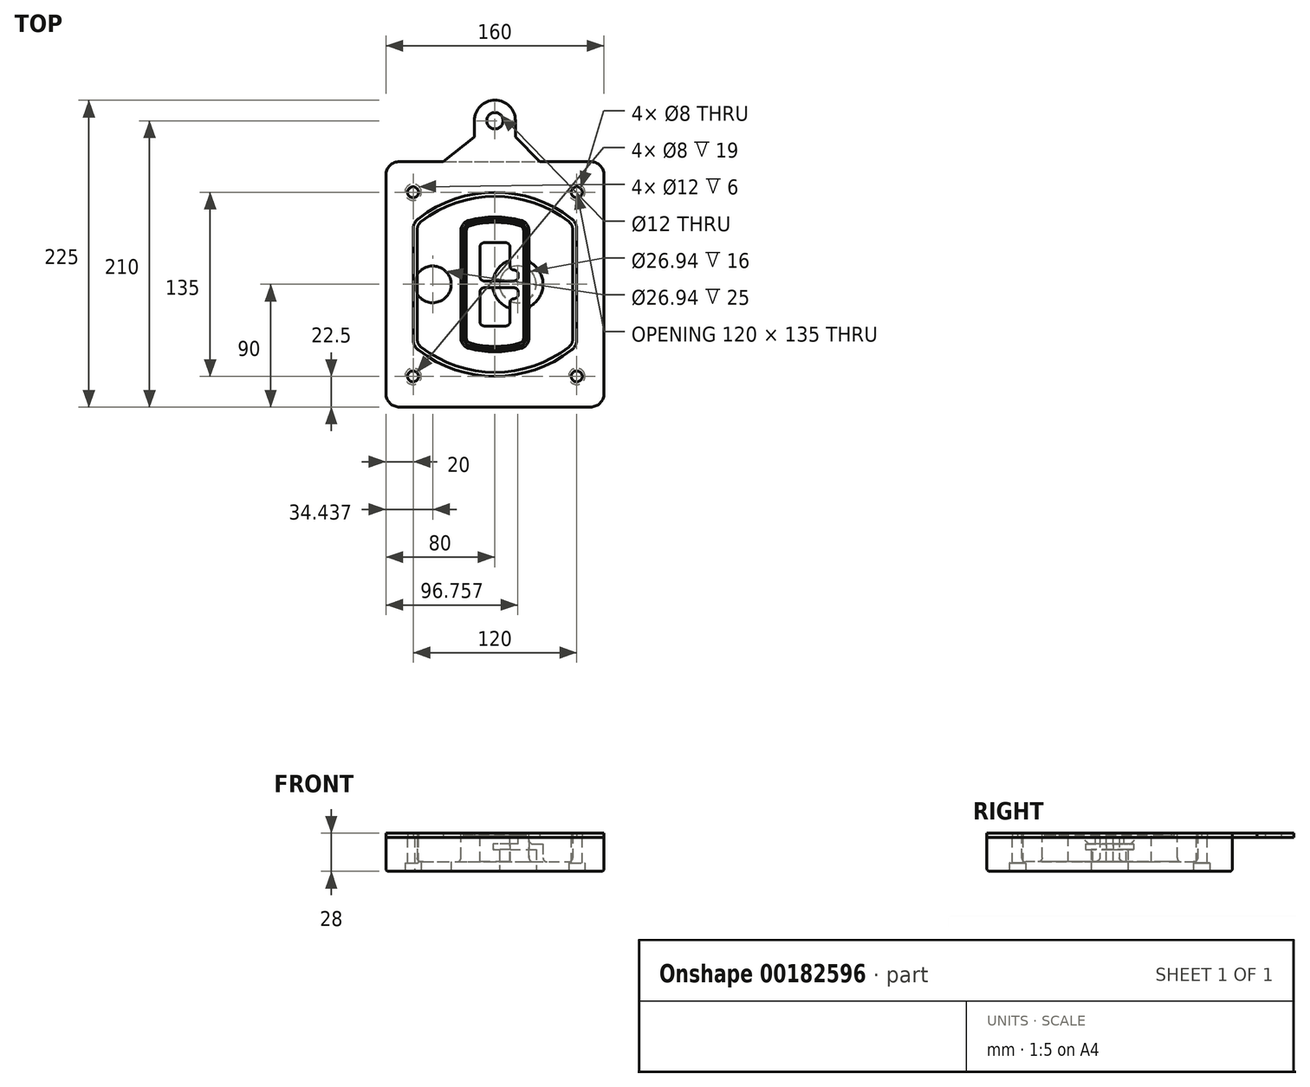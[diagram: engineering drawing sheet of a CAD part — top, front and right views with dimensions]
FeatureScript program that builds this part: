
annotation { "Feature Type Name" : "Feature", "Feature Type Description" : "" }
export const myFeature = defineFeature(function(context is Context, id is Id, definition is map)
    precondition{}
    {
        {
            var Q0;
            Q0=qCreatedBy(makeId("Top.planeOp"),FACE);
            var sketch = newSketch(context, id + "F0", { "sketchPlane" : qUnion([Q0])});
            skPoint(sketch, "E0.rect.middle", {"position": v(0, 0) * mm});
            skLineSegment(sketch, "E1.bottom", {"start": v(-70, -90) * mm, "end": v(70, -90) * mm});
            skLineSegment(sketch, "E1.top", {"start": v(-70, 90) * mm, "end": v(70, 90) * mm});
            skLineSegment(sketch, "E1.left", {"start": v(-80, -80) * mm, "end": v(-80, 80) * mm});
            skLineSegment(sketch, "E1.right", {"start": v(80, -80) * mm, "end": v(80, 80) * mm});
            skLineSegment(sketch, "E2", {"start": v(-80, 90) * mm, "end": v(80, -90) * mm, "construction": true});
            skLineSegment(sketch, "E3", {"start": v(80, 90) * mm, "end": v(-80, -90) * mm, "construction": true});
            skCircle(sketch, "E4", {"center": v(-60, 67.5) * mm, "radius": 4 * mm});
            skCircle(sketch, "E5", {"center": v(60, 67.5) * mm, "radius": 4 * mm});
            skCircle(sketch, "E6", {"center": v(60, -67.5) * mm, "radius": 4 * mm});
            skCircle(sketch, "E7", {"center": v(-60, -67.5) * mm, "radius": 4 * mm});
            skLineSegment(sketch, "E8", {"start": v(-60, 67.5) * mm, "end": v(60, 67.5) * mm, "construction": true});
            skLineSegment(sketch, "E9", {"start": v(60, 67.5) * mm, "end": v(60, -67.5) * mm, "construction": true});
            skLineSegment(sketch, "E10", {"start": v(60, -67.5) * mm, "end": v(-60, -67.5) * mm, "construction": true});
            skLineSegment(sketch, "E11", {"start": v(-60, -67.5) * mm, "end": v(-60, 67.5) * mm, "construction": true});
            skLineSegment(sketch, "E12", {"start": v(-60, 40.3) * mm, "end": v(-60, -40.3) * mm});
            skLineSegment(sketch, "E13", {"start": v(60, 40.3) * mm, "end": v(60, -40.3) * mm});
            skArc(sketch, "E14", {"start": v(56.15, 48.18) * mm, "mid": v(0, 67.5) * mm, "end": v(-56.15, 48.18) * mm});
            skArc(sketch, "E15", {"start": v(-56.15, -48.18) * mm, "mid": v(0, -67.5) * mm, "end": v(56.15, -48.18) * mm});
            skLineSegment(sketch, "E16", {"start": v(-60, 0) * mm, "end": v(60, 0) * mm, "construction": true});
            skPoint(sketch, "E17.visualSharp", {"position": v(-60, -45) * mm});
            skArc(sketch, "E17.filletArc", {"start": v(-60, -40.3) * mm, "mid": v(-58.99, -44.68) * mm, "end": v(-56.15, -48.18) * mm});
            skPoint(sketch, "E18.visualSharp", {"position": v(-60, 45) * mm});
            skArc(sketch, "E18.filletArc", {"start": v(-56.15, 48.18) * mm, "mid": v(-58.99, 44.68) * mm, "end": v(-60, 40.3) * mm});
            skPoint(sketch, "E19.visualSharp", {"position": v(60, 45) * mm});
            skArc(sketch, "E19.filletArc", {"start": v(60, 40.3) * mm, "mid": v(58.99, 44.68) * mm, "end": v(56.15, 48.18) * mm});
            skPoint(sketch, "E20.visualSharp", {"position": v(60, -45) * mm});
            skArc(sketch, "E20.filletArc", {"start": v(56.15, -48.18) * mm, "mid": v(58.99, -44.68) * mm, "end": v(60, -40.3) * mm});
            skPoint(sketch, "E21.visualSharp", {"position": v(-80, 90) * mm});
            skArc(sketch, "E21.filletArc", {"start": v(-70, 90) * mm, "mid": v(-77.07, 87.07) * mm, "end": v(-80, 80) * mm});
            skPoint(sketch, "E22.visualSharp", {"position": v(80, 90) * mm});
            skArc(sketch, "E22.filletArc", {"start": v(80, 80) * mm, "mid": v(77.07, 87.07) * mm, "end": v(70, 90) * mm});
            skPoint(sketch, "E23.visualSharp", {"position": v(80, -90) * mm});
            skArc(sketch, "E23.filletArc", {"start": v(70, -90) * mm, "mid": v(77.07, -87.07) * mm, "end": v(80, -80) * mm});
            skPoint(sketch, "E24.visualSharp", {"position": v(-80, -90) * mm});
            skArc(sketch, "E24.filletArc", {"start": v(-80, -80) * mm, "mid": v(-77.07, -87.07) * mm, "end": v(-70, -90) * mm});
            skArc(sketch, "E25.0", {"start": v(57, 40.3) * mm, "mid": v(56.3, 43.36) * mm, "end": v(54.3, 45.81) * mm});
            skLineSegment(sketch, "E25.1", {"start": v(57, 40.3) * mm, "end": v(57, -40.3) * mm});
            skArc(sketch, "E25.2", {"start": v(54.3, -45.81) * mm, "mid": v(56.3, -43.36) * mm, "end": v(57, -40.3) * mm});
            skArc(sketch, "E25.3", {"start": v(-54.3, -45.81) * mm, "mid": v(0, -64.5) * mm, "end": v(54.3, -45.81) * mm});
            skArc(sketch, "E25.4", {"start": v(-57, -40.3) * mm, "mid": v(-56.3, -43.36) * mm, "end": v(-54.3, -45.81) * mm});
            skArc(sketch, "E25.5", {"start": v(54.3, 45.81) * mm, "mid": v(0, 64.5) * mm, "end": v(-54.3, 45.81) * mm});
            skLineSegment(sketch, "E25.6", {"start": v(-57, 40.3) * mm, "end": v(-57, -40.3) * mm});
            skArc(sketch, "E25.7", {"start": v(-54.3, 45.81) * mm, "mid": v(-56.3, 43.36) * mm, "end": v(-57, 40.3) * mm});
            skArc(sketch, "E26.0", {"start": v(-58.62, 51.33) * mm, "mid": v(-62.58, 46.43) * mm, "end": v(-64, 40.3) * mm});
            skArc(sketch, "E26.1", {"start": v(58.62, 51.33) * mm, "mid": v(0, 71.5) * mm, "end": v(-58.62, 51.33) * mm});
            skArc(sketch, "E26.2", {"start": v(64, 40.3) * mm, "mid": v(62.58, 46.43) * mm, "end": v(58.62, 51.33) * mm});
            skLineSegment(sketch, "E26.3", {"start": v(64, 40.3) * mm, "end": v(64, -40.3) * mm});
            skArc(sketch, "E26.4", {"start": v(58.62, -51.33) * mm, "mid": v(62.58, -46.43) * mm, "end": v(64, -40.3) * mm});
            skLineSegment(sketch, "E26.5", {"start": v(-64, 40.3) * mm, "end": v(-64, -40.3) * mm});
            skArc(sketch, "E26.6", {"start": v(-58.62, -51.33) * mm, "mid": v(0, -71.5) * mm, "end": v(58.62, -51.33) * mm});
            skArc(sketch, "E26.7", {"start": v(-64, -40.3) * mm, "mid": v(-62.58, -46.43) * mm, "end": v(-58.62, -51.33) * mm});
            skSolve(sketch);
        }
        {
            var Q0;
            Q0=makeQuery(id+"F0.imprint","IMPRINT",FACE,{"disambiguationData":[TD([[makeQuery(id+"F0.imprint","IMPRINT",EDGE,{"derivedFrom":sQuery(id+"F0.wireOp",EDGE,"E1.bottom")}),1.0]])]});
            var Q1;
            Q1=makeQuery(id+"F0.imprint","IMPRINT",FACE,{"disambiguationData":[TD([[makeQuery(id+"F0.imprint","IMPRINT",EDGE,{"derivedFrom":sQuery(id+"F0.wireOp",EDGE,"E12")}),1.0]])]});
            var Q2;
            Q2=makeQuery(id+"F0.imprint","IMPRINT",FACE,{"disambiguationData":[TD([[makeQuery(id+"F0.imprint","IMPRINT",EDGE,{"derivedFrom":sQuery(id+"F0.wireOp",EDGE,"E25.0")}),1.0]])]});
            var Q3;
            Q3=makeQuery(id+"F0.imprint","IMPRINT",FACE,{"disambiguationData":[TD([[makeQuery(id+"F0.imprint","IMPRINT",EDGE,{"derivedFrom":sQuery(id+"F0.wireOp",EDGE,"E12")}),-1.0]])]});
            extrude(context, id + "F1", {"entities" : qUnion([Q0, Q1, Q2, Q3]), "oppositeDirection" : true, "depth" : 25 * mm});
        }
        {
            var Q0;
            Q0=makeQuery(id+"F0.imprint","IMPRINT",FACE,{"disambiguationData":[TD([[makeQuery(id+"F0.imprint","IMPRINT",EDGE,{"derivedFrom":sQuery(id+"F0.wireOp",EDGE,"E12")}),1.0]])]});
            extrude(context, id + "F2", {"entities" : qUnion([Q0]), "operationType" : NewBodyOperationType.ADD, "depth" : 3 * mm});
        }
        {
            var Q0;
            Q0=makeQuery(id+"F0.imprint","IMPRINT",FACE,{"disambiguationData":[TD([[makeQuery(id+"F0.imprint","IMPRINT",EDGE,{"derivedFrom":sQuery(id+"F0.wireOp",EDGE,"E25.0")}),1.0]])]});
            extrude(context, id + "F3", {"entities" : qUnion([Q0]), "operationType" : NewBodyOperationType.REMOVE, "oppositeDirection" : true, "depth" : 18 * mm});
        }
        {
            var Q0;
            Q0=makeQuery(id+"F2.opExtrude","CAP_FACE",FACE,{"disambiguationData":[OSD([sQuery(id+"F0.wireOp",EDGE,"E12"),sQuery(id+"F0.wireOp",EDGE,"E13"),sQuery(id+"F0.wireOp",EDGE,"E14"),sQuery(id+"F0.wireOp",EDGE,"E15"),sQuery(id+"F0.wireOp",EDGE,"E17.filletArc"),sQuery(id+"F0.wireOp",EDGE,"E18.filletArc"),sQuery(id+"F0.wireOp",EDGE,"E19.filletArc"),sQuery(id+"F0.wireOp",EDGE,"E20.filletArc"),sQuery(id+"F0.wireOp",EDGE,"E25.0"),sQuery(id+"F0.wireOp",EDGE,"E25.1"),sQuery(id+"F0.wireOp",EDGE,"E25.2"),sQuery(id+"F0.wireOp",EDGE,"E25.3"),sQuery(id+"F0.wireOp",EDGE,"E25.4"),sQuery(id+"F0.wireOp",EDGE,"E25.5"),sQuery(id+"F0.wireOp",EDGE,"E25.6"),sQuery(id+"F0.wireOp",EDGE,"E25.7")])],"isStart":false});
            var sketch = newSketch(context, id + "F4", { "sketchPlane" : qUnion([Q0])});
            skArc(sketch, "E27.0", {"start": v(-19.08, -46.97) * mm, "mid": v(0, -49.5) * mm, "end": v(19.08, -46.97) * mm});
            skArc(sketch, "E28.0", {"start": v(19.08, 46.97) * mm, "mid": v(0, 49.5) * mm, "end": v(-19.08, 46.97) * mm});
            skLineSegment(sketch, "E29", {"start": v(-25, 39.25) * mm, "end": v(-25, -39.25) * mm});
            skLineSegment(sketch, "E30", {"start": v(25, 39.25) * mm, "end": v(25, -39.25) * mm});
            skLineSegment(sketch, "E31", {"start": v(-25, 45.1) * mm, "end": v(25, 45.1) * mm, "construction": true});
            skLineSegment(sketch, "E32", {"start": v(-25, -45.1) * mm, "end": v(25, -45.1) * mm, "construction": true});
            skPoint(sketch, "E33.visualSharp", {"position": v(-25, 45.1) * mm});
            skArc(sketch, "E33.filletArc", {"start": v(-19.08, 46.97) * mm, "mid": v(-23.35, 44.11) * mm, "end": v(-25, 39.25) * mm});
            skPoint(sketch, "E34.visualSharp", {"position": v(25, 45.1) * mm});
            skArc(sketch, "E34.filletArc", {"start": v(25, 39.25) * mm, "mid": v(23.35, 44.11) * mm, "end": v(19.08, 46.97) * mm});
            skPoint(sketch, "E35.visualSharp", {"position": v(25, -45.1) * mm});
            skArc(sketch, "E35.filletArc", {"start": v(19.08, -46.97) * mm, "mid": v(23.35, -44.11) * mm, "end": v(25, -39.25) * mm});
            skPoint(sketch, "E36.visualSharp", {"position": v(-25, -45.1) * mm});
            skArc(sketch, "E36.filletArc", {"start": v(-25, -39.25) * mm, "mid": v(-23.35, -44.11) * mm, "end": v(-19.08, -46.97) * mm});
            skArc(sketch, "E37.0", {"start": v(54.3, 45.81) * mm, "mid": v(0, 64.5) * mm, "end": v(-54.3, 45.81) * mm});
            skArc(sketch, "E37.1", {"start": v(-54.3, 45.81) * mm, "mid": v(-56.3, 43.36) * mm, "end": v(-57, 40.3) * mm});
            skLineSegment(sketch, "E37.2", {"start": v(-57, 40.3) * mm, "end": v(-57, -40.3) * mm});
            skArc(sketch, "E37.3", {"start": v(-57, -40.3) * mm, "mid": v(-56.3, -43.36) * mm, "end": v(-54.3, -45.81) * mm});
            skArc(sketch, "E37.4", {"start": v(-54.3, -45.81) * mm, "mid": v(0, -64.5) * mm, "end": v(54.3, -45.81) * mm});
            skArc(sketch, "E37.5", {"start": v(54.3, -45.81) * mm, "mid": v(56.3, -43.36) * mm, "end": v(57, -40.3) * mm});
            skLineSegment(sketch, "E37.6", {"start": v(57, 40.3) * mm, "end": v(57, -40.3) * mm});
            skArc(sketch, "E37.7", {"start": v(57, 40.3) * mm, "mid": v(56.3, 43.36) * mm, "end": v(54.3, 45.81) * mm});
            skLineSegment(sketch, "E38.0", {"start": v(23, 39.25) * mm, "end": v(23, -39.25) * mm});
            skArc(sketch, "E38.1", {"start": v(18.56, -45.04) * mm, "mid": v(21.76, -42.9) * mm, "end": v(23, -39.25) * mm});
            skArc(sketch, "E38.2", {"start": v(-18.56, -45.04) * mm, "mid": v(0, -47.5) * mm, "end": v(18.56, -45.04) * mm});
            skArc(sketch, "E38.3", {"start": v(-23, -39.25) * mm, "mid": v(-21.76, -42.9) * mm, "end": v(-18.56, -45.04) * mm});
            skLineSegment(sketch, "E38.4", {"start": v(-23, 39.25) * mm, "end": v(-23, -39.25) * mm});
            skArc(sketch, "E38.5", {"start": v(23, 39.25) * mm, "mid": v(21.76, 42.9) * mm, "end": v(18.56, 45.04) * mm});
            skArc(sketch, "E38.6", {"start": v(-18.56, 45.04) * mm, "mid": v(-21.76, 42.9) * mm, "end": v(-23, 39.25) * mm});
            skArc(sketch, "E38.7", {"start": v(18.56, 45.04) * mm, "mid": v(0, 47.5) * mm, "end": v(-18.56, 45.04) * mm});
            skArc(sketch, "E39.0", {"start": v(21, 39.25) * mm, "mid": v(20.18, 41.68) * mm, "end": v(18.04, 43.1) * mm});
            skLineSegment(sketch, "E39.1", {"start": v(21, 39.25) * mm, "end": v(21, -39.25) * mm});
            skArc(sketch, "E39.2", {"start": v(18.04, -43.1) * mm, "mid": v(20.18, -41.68) * mm, "end": v(21, -39.25) * mm});
            skArc(sketch, "E39.3", {"start": v(-18.04, -43.1) * mm, "mid": v(0, -45.5) * mm, "end": v(18.04, -43.1) * mm});
            skArc(sketch, "E39.4", {"start": v(-21, -39.25) * mm, "mid": v(-20.18, -41.68) * mm, "end": v(-18.04, -43.1) * mm});
            skArc(sketch, "E39.5", {"start": v(18.04, 43.1) * mm, "mid": v(0, 45.5) * mm, "end": v(-18.04, 43.1) * mm});
            skLineSegment(sketch, "E39.6", {"start": v(-21, 39.25) * mm, "end": v(-21, -39.25) * mm});
            skArc(sketch, "E39.7", {"start": v(-18.04, 43.1) * mm, "mid": v(-20.18, 41.68) * mm, "end": v(-21, 39.25) * mm});
            skLineSegment(sketch, "E40", {"start": v(-25, 0) * mm, "end": v(25, 0) * mm, "construction": true});
            skLineSegment(sketch, "E41", {"start": v(-11, 5.5) * mm, "end": v(-11, 27.5) * mm});
            skLineSegment(sketch, "E42", {"start": v(-8, 30.5) * mm, "end": v(8, 30.5) * mm});
            skLineSegment(sketch, "E43", {"start": v(11, 27.5) * mm, "end": v(11, 13.5) * mm});
            skLineSegment(sketch, "E44", {"start": v(14, 10.5) * mm, "end": v(14, 10.5) * mm});
            skLineSegment(sketch, "E45", {"start": v(17, 7.5) * mm, "end": v(17, 5.5) * mm});
            skLineSegment(sketch, "E46", {"start": v(14, 2.5) * mm, "end": v(-8, 2.5) * mm});
            skPoint(sketch, "E47.visualSharp", {"position": v(-11, 30.5) * mm});
            skArc(sketch, "E47.filletArc", {"start": v(-8, 30.5) * mm, "mid": v(-10.12, 29.62) * mm, "end": v(-11, 27.5) * mm});
            skPoint(sketch, "E48.visualSharp", {"position": v(11, 30.5) * mm});
            skArc(sketch, "E48.filletArc", {"start": v(11, 27.5) * mm, "mid": v(10.12, 29.62) * mm, "end": v(8, 30.5) * mm});
            skPoint(sketch, "E49.visualSharp", {"position": v(11, 10.5) * mm});
            skArc(sketch, "E49.filletArc", {"start": v(11, 13.5) * mm, "mid": v(11.88, 11.38) * mm, "end": v(14, 10.5) * mm});
            skPoint(sketch, "E50.visualSharp", {"position": v(17, 10.5) * mm});
            skArc(sketch, "E50.filletArc", {"start": v(17, 7.5) * mm, "mid": v(16.12, 9.62) * mm, "end": v(14, 10.5) * mm});
            skPoint(sketch, "E51.visualSharp", {"position": v(17, 2.5) * mm});
            skArc(sketch, "E51.filletArc", {"start": v(14, 2.5) * mm, "mid": v(16.12, 3.38) * mm, "end": v(17, 5.5) * mm});
            skPoint(sketch, "E52.visualSharp", {"position": v(-11, 2.5) * mm});
            skArc(sketch, "E52.filletArc", {"start": v(-11, 5.5) * mm, "mid": v(-10.12, 3.38) * mm, "end": v(-8, 2.5) * mm});
            skLineSegment(sketch, "E53.0.MirrorCS", {"start": v(14, -2.5) * mm, "end": v(-8, -2.5) * mm});
            skArc(sketch, "E54.0.MirrorCS", {"start": v(-11, -5.5) * mm, "mid": v(-10.12, -3.38) * mm, "end": v(-8, -2.5) * mm});
            skLineSegment(sketch, "E55.0.MirrorCS", {"start": v(-11, -5.5) * mm, "end": v(-11, -27.5) * mm});
            skArc(sketch, "E56.0.MirrorCS", {"start": v(-8, -30.5) * mm, "mid": v(-10.12, -29.62) * mm, "end": v(-11, -27.5) * mm});
            skLineSegment(sketch, "E57.0.MirrorCS", {"start": v(-8, -30.5) * mm, "end": v(8, -30.5) * mm});
            skArc(sketch, "E58.0.MirrorCS", {"start": v(11, -27.5) * mm, "mid": v(10.12, -29.62) * mm, "end": v(8, -30.5) * mm});
            skLineSegment(sketch, "E59.0.MirrorCS", {"start": v(11, -27.5) * mm, "end": v(11, -13.5) * mm});
            skArc(sketch, "E60.0.MirrorCS", {"start": v(11, -13.5) * mm, "mid": v(11.88, -11.38) * mm, "end": v(14, -10.5) * mm});
            skArc(sketch, "E61.0.MirrorCS", {"start": v(17, -7.5) * mm, "mid": v(16.12, -9.62) * mm, "end": v(14, -10.5) * mm});
            skLineSegment(sketch, "E62.0.MirrorCS", {"start": v(17, -7.5) * mm, "end": v(17, -5.5) * mm});
            skArc(sketch, "E63.0.MirrorCS", {"start": v(14, -2.5) * mm, "mid": v(16.12, -3.38) * mm, "end": v(17, -5.5) * mm});
            skSolve(sketch);
        }
        {
            var Q0;
            Q0=makeQuery(id+"F4.imprint","IMPRINT",FACE,{"disambiguationData":[TD([[makeQuery(id+"F4.imprint","IMPRINT",EDGE,{"derivedFrom":sQuery(id+"F4.wireOp",EDGE,"E27.0")}),1.0]])]});
            var Q1;
            Q1=makeQuery(id+"F4.imprint","IMPRINT",FACE,{"disambiguationData":[TD([[makeQuery(id+"F4.imprint","IMPRINT",EDGE,{"derivedFrom":sQuery(id+"F4.wireOp",EDGE,"E38.0")}),-1.0]])]});
            var Q2;
            Q2=makeQuery(id+"F4.imprint","IMPRINT",FACE,{"disambiguationData":[TD([[makeQuery(id+"F4.imprint","IMPRINT",EDGE,{"derivedFrom":sQuery(id+"F4.wireOp",EDGE,"E39.0")}),1.0]])]});
            extrude(context, id + "F5", {"entities" : qUnion([Q0, Q1, Q2]), "operationType" : NewBodyOperationType.ADD, "endBound" : BoundingType.UP_TO_NEXT, "oppositeDirection" : true, "depth" : 25 * mm});
        }
        {
            var Q0;
            Q0=makeQuery(id+"F4.imprint","IMPRINT",FACE,{"disambiguationData":[TD([[makeQuery(id+"F4.imprint","IMPRINT",EDGE,{"derivedFrom":sQuery(id+"F4.wireOp",EDGE,"E38.0")}),-1.0]])]});
            extrude(context, id + "F6", {"entities" : qUnion([Q0]), "operationType" : NewBodyOperationType.REMOVE, "oppositeDirection" : true, "depth" : 2 * mm});
        }
        {
            var Q0;
            Q0=makeQuery(id+"F1.opExtrude","CAP_FACE",FACE,{"disambiguationData":[OSD([sQuery(id+"F0.wireOp",EDGE,"E1.bottom"),sQuery(id+"F0.wireOp",EDGE,"E1.top"),sQuery(id+"F0.wireOp",EDGE,"E1.left"),sQuery(id+"F0.wireOp",EDGE,"E1.right"),sQuery(id+"F0.wireOp",EDGE,"E4"),sQuery(id+"F0.wireOp",EDGE,"E5"),sQuery(id+"F0.wireOp",EDGE,"E6"),sQuery(id+"F0.wireOp",EDGE,"E7"),sQuery(id+"F0.wireOp",EDGE,"E21.filletArc"),sQuery(id+"F0.wireOp",EDGE,"E22.filletArc"),sQuery(id+"F0.wireOp",EDGE,"E23.filletArc"),sQuery(id+"F0.wireOp",EDGE,"E24.filletArc")])],"isStart":false});
            var sketch = newSketch(context, id + "F7", { "sketchPlane" : qUnion([Q0])});
            skCircle(sketch, "E64", {"center": v(16.76, 0) * mm, "radius": 13.47 * mm});
            skCircle(sketch, "E65", {"center": v(-45.56, 0) * mm, "radius": 13.47 * mm});
            skLineSegment(sketch, "E66", {"start": v(80, 0) * mm, "end": v(-80, 0) * mm});
            skCircle(sketch, "E67", {"center": v(16.76, 0) * mm, "radius": 18.47 * mm});
            skCircle(sketch, "E68", {"center": v(60, -67.5) * mm, "radius": 6 * mm});
            skCircle(sketch, "E69", {"center": v(-60, -67.5) * mm, "radius": 6 * mm});
            skCircle(sketch, "E70", {"center": v(-60, 67.5) * mm, "radius": 6 * mm});
            skCircle(sketch, "E71", {"center": v(60, 67.5) * mm, "radius": 6 * mm});
            skSolve(sketch);
        }
        {
            var Q0;
            {var subQ1=sQuery(id+"F7.wireOp",EDGE,"E66");var subQ4=sQuery(id+"F7.wireOp",EDGE,"E64");var subQ6=makeQuery(id+"F7.imprint","INTERSECT",VERTEX,{"disambiguationData":[OD(0.0)],"derivedFrom":[subQ4,subQ1]});Q0=makeQuery(id+"F7.imprint","IMPRINT",FACE,{"disambiguationData":[TD([[makeQuery(id+"F7.imprint","IMPRINT",EDGE,{"disambiguationData":[TD([[subQ6,-1.0]])],"derivedFrom":subQ4}),-1.0]])]});}
            var Q1;
            {var subQ0=sQuery(id+"F7.wireOp",EDGE,"E66");var subQ1=sQuery(id+"F7.wireOp",EDGE,"E64");var subQ3=makeQuery(id+"F7.imprint","INTERSECT",VERTEX,{"disambiguationData":[OD(0.0)],"derivedFrom":[subQ1,subQ0]});Q1=makeQuery(id+"F7.imprint","IMPRINT",FACE,{"disambiguationData":[TD([[makeQuery(id+"F7.imprint","IMPRINT",EDGE,{"disambiguationData":[TD([[subQ3,-1.0]])],"derivedFrom":subQ1}),1.0]])]});}
            var Q2;
            {var subQ0=sQuery(id+"F7.wireOp",EDGE,"E66");var subQ1=sQuery(id+"F7.wireOp",EDGE,"E64");var subQ3=makeQuery(id+"F7.imprint","INTERSECT",VERTEX,{"disambiguationData":[OD(0.0)],"derivedFrom":[subQ1,subQ0]});Q2=makeQuery(id+"F7.imprint","IMPRINT",FACE,{"disambiguationData":[TD([[makeQuery(id+"F7.imprint","IMPRINT",EDGE,{"disambiguationData":[TD([[subQ3,1.0]])],"derivedFrom":subQ1}),1.0]])]});}
            var Q3;
            {var subQ1=sQuery(id+"F7.wireOp",EDGE,"E66");var subQ4=sQuery(id+"F7.wireOp",EDGE,"E64");var subQ6=makeQuery(id+"F7.imprint","INTERSECT",VERTEX,{"disambiguationData":[OD(0.0)],"derivedFrom":[subQ4,subQ1]});Q3=makeQuery(id+"F7.imprint","IMPRINT",FACE,{"disambiguationData":[TD([[makeQuery(id+"F7.imprint","IMPRINT",EDGE,{"disambiguationData":[TD([[subQ6,1.0]])],"derivedFrom":subQ4}),-1.0]])]});}
            extrude(context, id + "F8", {"entities" : qUnion([Q0, Q1, Q2, Q3]), "operationType" : NewBodyOperationType.ADD, "oppositeDirection" : true, "depth" : 20 * mm});
        }
        {
            var Q0;
            {var subQ0=sQuery(id+"F7.wireOp",EDGE,"E66");var subQ1=sQuery(id+"F7.wireOp",EDGE,"E64");var subQ3=makeQuery(id+"F7.imprint","INTERSECT",VERTEX,{"disambiguationData":[OD(0.0)],"derivedFrom":[subQ1,subQ0]});Q0=makeQuery(id+"F7.imprint","IMPRINT",FACE,{"disambiguationData":[TD([[makeQuery(id+"F7.imprint","IMPRINT",EDGE,{"disambiguationData":[TD([[subQ3,-1.0]])],"derivedFrom":subQ1}),1.0]])]});}
            var Q1;
            {var subQ0=sQuery(id+"F7.wireOp",EDGE,"E66");var subQ1=sQuery(id+"F7.wireOp",EDGE,"E64");var subQ3=makeQuery(id+"F7.imprint","INTERSECT",VERTEX,{"disambiguationData":[OD(0.0)],"derivedFrom":[subQ1,subQ0]});Q1=makeQuery(id+"F7.imprint","IMPRINT",FACE,{"disambiguationData":[TD([[makeQuery(id+"F7.imprint","IMPRINT",EDGE,{"disambiguationData":[TD([[subQ3,1.0]])],"derivedFrom":subQ1}),1.0]])]});}
            extrude(context, id + "F9", {"entities" : qUnion([Q0, Q1]), "operationType" : NewBodyOperationType.REMOVE, "oppositeDirection" : true, "depth" : 16 * mm});
        }
        {
            var Q0;
            {var subQ0=sQuery(id+"F7.wireOp",EDGE,"E66");var subQ1=sQuery(id+"F7.wireOp",EDGE,"E65");var subQ3=makeQuery(id+"F7.imprint","INTERSECT",VERTEX,{"disambiguationData":[OD(0.0)],"derivedFrom":[subQ1,subQ0]});Q0=makeQuery(id+"F7.imprint","IMPRINT",FACE,{"disambiguationData":[TD([[makeQuery(id+"F7.imprint","IMPRINT",EDGE,{"disambiguationData":[TD([[subQ3,-1.0]])],"derivedFrom":subQ1}),1.0]])]});}
            var Q1;
            {var subQ0=sQuery(id+"F7.wireOp",EDGE,"E66");var subQ1=sQuery(id+"F7.wireOp",EDGE,"E65");var subQ3=makeQuery(id+"F7.imprint","INTERSECT",VERTEX,{"disambiguationData":[OD(0.0)],"derivedFrom":[subQ1,subQ0]});Q1=makeQuery(id+"F7.imprint","IMPRINT",FACE,{"disambiguationData":[TD([[makeQuery(id+"F7.imprint","IMPRINT",EDGE,{"disambiguationData":[TD([[subQ3,1.0]])],"derivedFrom":subQ1}),1.0]])]});}
            extrude(context, id + "F10", {"entities" : qUnion([Q0, Q1]), "operationType" : NewBodyOperationType.REMOVE, "oppositeDirection" : true, "depth" : 25 * mm});
        }
        {
            var Q0;
            Q0=makeQuery(id+"F7.imprint","IMPRINT",FACE,{"disambiguationData":[TD([[makeQuery(id+"F7.imprint","IMPRINT",EDGE,{"derivedFrom":sQuery(id+"F7.wireOp",EDGE,"E68")}),1.0]])]});
            var Q1;
            Q1=makeQuery(id+"F7.imprint","IMPRINT",FACE,{"disambiguationData":[TD([[makeQuery(id+"F7.imprint","IMPRINT",EDGE,{"derivedFrom":makeQuery(id+"F1.opExtrude","CAP_EDGE",EDGE,{"disambiguationData":[OSD([sQuery(id+"F0.wireOp",EDGE,"E5")])],"isStart":false})}),-1.0]])]});
            var Q2;
            Q2=makeQuery(id+"F7.imprint","IMPRINT",FACE,{"disambiguationData":[TD([[makeQuery(id+"F7.imprint","IMPRINT",EDGE,{"derivedFrom":sQuery(id+"F7.wireOp",EDGE,"E69")}),1.0]])]});
            var Q3;
            Q3=makeQuery(id+"F7.imprint","IMPRINT",FACE,{"disambiguationData":[TD([[makeQuery(id+"F7.imprint","IMPRINT",EDGE,{"derivedFrom":makeQuery(id+"F1.opExtrude","CAP_EDGE",EDGE,{"disambiguationData":[OSD([sQuery(id+"F0.wireOp",EDGE,"E4")])],"isStart":false})}),-1.0]])]});
            var Q4;
            Q4=makeQuery(id+"F7.imprint","IMPRINT",FACE,{"disambiguationData":[TD([[makeQuery(id+"F7.imprint","IMPRINT",EDGE,{"derivedFrom":sQuery(id+"F7.wireOp",EDGE,"E70")}),1.0]])]});
            var Q5;
            Q5=makeQuery(id+"F7.imprint","IMPRINT",FACE,{"disambiguationData":[TD([[makeQuery(id+"F7.imprint","IMPRINT",EDGE,{"derivedFrom":makeQuery(id+"F1.opExtrude","CAP_EDGE",EDGE,{"disambiguationData":[OSD([sQuery(id+"F0.wireOp",EDGE,"E7")])],"isStart":false})}),-1.0]])]});
            var Q6;
            Q6=makeQuery(id+"F7.imprint","IMPRINT",FACE,{"disambiguationData":[TD([[makeQuery(id+"F7.imprint","IMPRINT",EDGE,{"derivedFrom":sQuery(id+"F7.wireOp",EDGE,"E71")}),1.0]])]});
            var Q7;
            Q7=makeQuery(id+"F7.imprint","IMPRINT",FACE,{"disambiguationData":[TD([[makeQuery(id+"F7.imprint","IMPRINT",EDGE,{"derivedFrom":makeQuery(id+"F1.opExtrude","CAP_EDGE",EDGE,{"disambiguationData":[OSD([sQuery(id+"F0.wireOp",EDGE,"E6")])],"isStart":false})}),-1.0]])]});
            extrude(context, id + "F11", {"entities" : qUnion([Q0, Q1, Q2, Q3, Q4, Q5, Q6, Q7]), "operationType" : NewBodyOperationType.REMOVE, "oppositeDirection" : true, "depth" : 6 * mm});
        }
        {
            var Q0;
            Q0=makeQuery(id+"F9.boolean.opBoolean","COPY",FACE,{"derivedFrom":makeQuery(id+"F9.opExtrude","CAP_FACE",FACE,{"disambiguationData":[OSD([sQuery(id+"F7.wireOp",EDGE,"E64")])],"isStart":false})});
            var sketch = newSketch(context, id + "F12", { "sketchPlane" : qUnion([Q0])});
            skArc(sketch, "E72.0", {"start": v(11, 17.55) * mm, "mid": v(2.57, 11.82) * mm, "end": v(-1.54, 2.5) * mm});
            skArc(sketch, "E72.1", {"start": v(-1.54, -2.5) * mm, "mid": v(2.57, -11.82) * mm, "end": v(11, -17.55) * mm});
            skLineSegment(sketch, "E73", {"start": v(-1.54, -2.5) * mm, "end": v(14, -2.5) * mm});
            skLineSegment(sketch, "E74.0", {"start": v(14, 2.5) * mm, "end": v(-1.54, 2.5) * mm});
            skArc(sketch, "E74.1", {"start": v(14, 2.5) * mm, "mid": v(16.12, 3.38) * mm, "end": v(17, 5.5) * mm});
            skLineSegment(sketch, "E74.2", {"start": v(17, 7.5) * mm, "end": v(17, 5.5) * mm});
            skArc(sketch, "E74.3", {"start": v(17, 7.5) * mm, "mid": v(16.12, 9.62) * mm, "end": v(14, 10.5) * mm});
            skArc(sketch, "E74.4", {"start": v(11, 13.5) * mm, "mid": v(11.88, 11.38) * mm, "end": v(14, 10.5) * mm});
            skLineSegment(sketch, "E74.5", {"start": v(11, 17.55) * mm, "end": v(11, 13.5) * mm});
            skLineSegment(sketch, "E74.7", {"start": v(14, -2.5) * mm, "end": v(-1.54, -2.5) * mm});
            skArc(sketch, "E74.8", {"start": v(14, -2.5) * mm, "mid": v(16.12, -3.38) * mm, "end": v(17, -5.5) * mm});
            skLineSegment(sketch, "E74.9", {"start": v(17, -7.5) * mm, "end": v(17, -5.5) * mm});
            skArc(sketch, "E74.10", {"start": v(17, -7.5) * mm, "mid": v(16.12, -9.62) * mm, "end": v(14, -10.5) * mm});
            skArc(sketch, "E74.11", {"start": v(11, -13.5) * mm, "mid": v(11.88, -11.38) * mm, "end": v(14, -10.5) * mm});
            skLineSegment(sketch, "E74.12", {"start": v(11, -17.55) * mm, "end": v(11, -13.5) * mm});
            skPoint(sketch, "E75.orphan", {"position": v(11, -27.5) * mm});
            skPoint(sketch, "E76.orphan", {"position": v(-8, -2.5) * mm});
            skPoint(sketch, "E77.orphan", {"position": v(-8, 2.5) * mm});
            skPoint(sketch, "E78.orphan", {"position": v(11, 27.5) * mm});
            skSolve(sketch);
        }
        {
            var Q0;
            {var subQ7=sQuery(id+"F12.wireOp",EDGE,"E72.0");var subQ14=sQuery(id+"F12.wireOp",EDGE,"E72.1");var subQ16=sQuery(id+"F12.wireOp",EDGE,"E74.1");var subQ18=sQuery(id+"F12.wireOp",EDGE,"E74.8");Q0=qUnion([makeQuery(id+"F12.imprint","IMPRINT",FACE,{"disambiguationData":[TD([[makeQuery(id+"F12.imprint","IMPRINT",EDGE,{"derivedFrom":subQ7}),1.0]])]}),makeQuery(id+"F12.imprint","IMPRINT",FACE,{"disambiguationData":[TD([[makeQuery(id+"F12.imprint","IMPRINT",EDGE,{"derivedFrom":subQ14}),1.0]])]}),makeQuery(id+"F12.imprint","IMPRINT",FACE,{"disambiguationData":[TD([[makeQuery(id+"F12.imprint","IMPRINT",EDGE,{"derivedFrom":subQ16}),1.0]])]}),makeQuery(id+"F12.imprint","IMPRINT",FACE,{"disambiguationData":[TD([[makeQuery(id+"F12.imprint","IMPRINT",EDGE,{"derivedFrom":subQ18}),-1.0]])]})]);}
            var Q1;
            Q1=makeQuery(id+"F5.boolean.opBoolean","SPLIT",FACE,{"disambiguationData":[TD([makeQuery(id+"F5.opExtrude","SWEPT_FACE",FACE,{"disambiguationData":[OSD([sQuery(id+"F4.wireOp",EDGE,"E41")])]})])],"derivedFrom":makeQuery(id+"F3.boolean.opBoolean","COPY",FACE,{"derivedFrom":makeQuery(id+"F3.opExtrude","CAP_FACE",FACE,{"disambiguationData":[OSD([sQuery(id+"F0.wireOp",EDGE,"E25.0"),sQuery(id+"F0.wireOp",EDGE,"E25.1"),sQuery(id+"F0.wireOp",EDGE,"E25.2"),sQuery(id+"F0.wireOp",EDGE,"E25.3"),sQuery(id+"F0.wireOp",EDGE,"E25.4"),sQuery(id+"F0.wireOp",EDGE,"E25.5"),sQuery(id+"F0.wireOp",EDGE,"E25.6"),sQuery(id+"F0.wireOp",EDGE,"E25.7")])],"isStart":false})})});
            extrude(context, id + "F13", {"entities" : qUnion([Q0]), "operationType" : NewBodyOperationType.REMOVE, "endBound" : BoundingType.UP_TO_SURFACE, "endBoundEntityFace" : qUnion([Q1]), "depth" : 25 * mm});
        }
        {
            var Q0;
            Q0=makeQuery(id+"F3.boolean.opBoolean","COPY",EDGE,{"derivedFrom":makeQuery(id+"F3.opExtrude","CAP_EDGE",EDGE,{"disambiguationData":[OSD([sQuery(id+"F0.wireOp",EDGE,"E25.6")])],"isStart":false})});
            var Q1;
            Q1=makeQuery(id+"F8.boolean.opBoolean","INTERSECT",EDGE,{"derivedFrom":[makeQuery(id+"F5.opExtrude","SWEPT_FACE",FACE,{"disambiguationData":[OSD([sQuery(id+"F4.wireOp",EDGE,"E30")])]}),makeQuery(id+"F8.opExtrude","CAP_FACE",FACE,{"disambiguationData":[OSD([sQuery(id+"F7.wireOp",EDGE,"E67")])],"isStart":false})]});
            var Q2;
            Q2=makeQuery(id+"F8.boolean.opBoolean","INTERSECT",EDGE,{"disambiguationData":[OD(1.0)],"derivedFrom":[makeQuery(id+"F5.opExtrude","SWEPT_FACE",FACE,{"disambiguationData":[OSD([sQuery(id+"F4.wireOp",EDGE,"E30")])]}),makeQuery(id+"F8.opExtrude","SWEPT_FACE",FACE,{"disambiguationData":[OSD([sQuery(id+"F7.wireOp",EDGE,"E67")])]})]});
            var Q3;
            {var subQ0=sQuery(id+"F4.wireOp",EDGE,"E30");Q3=makeQuery(id+"F8.boolean.opBoolean","SPLIT",EDGE,{"disambiguationData":[TD([makeQuery(id+"F5.opExtrude","SWEPT_FACE",FACE,{"disambiguationData":[OSD([sQuery(id+"F4.wireOp",EDGE,"E35.filletArc")])]})])],"derivedFrom":makeQuery(id+"F5.opExtrude","CAP_EDGE",EDGE,{"disambiguationData":[OSD([subQ0])],"isStart":false})});}
            var Q4;
            {var subQ0=sQuery(id+"F0.wireOp",EDGE,"E25.7");var subQ1=sQuery(id+"F0.wireOp",EDGE,"E25.1");var subQ2=sQuery(id+"F0.wireOp",EDGE,"E25.6");var subQ3=sQuery(id+"F0.wireOp",EDGE,"E25.5");var subQ4=sQuery(id+"F0.wireOp",EDGE,"E25.4");var subQ5=sQuery(id+"F0.wireOp",EDGE,"E25.0");var subQ6=sQuery(id+"F0.wireOp",EDGE,"E25.2");var subQ7=sQuery(id+"F0.wireOp",EDGE,"E25.3");Q4=makeQuery(id+"F8.boolean.opBoolean","INTERSECT",EDGE,{"derivedFrom":[makeQuery(id+"F5.boolean.opBoolean","SPLIT",FACE,{"disambiguationData":[TD([makeQuery(id+"F2.opExtrude","SWEPT_FACE",FACE,{"disambiguationData":[OSD([subQ5])]})])],"derivedFrom":makeQuery(id+"F3.boolean.opBoolean","COPY",FACE,{"derivedFrom":makeQuery(id+"F3.opExtrude","CAP_FACE",FACE,{"disambiguationData":[OSD([subQ5,subQ1,subQ6,subQ7,subQ4,subQ3,subQ2,subQ0])],"isStart":false})})}),makeQuery(id+"F8.opExtrude","SWEPT_FACE",FACE,{"disambiguationData":[OSD([sQuery(id+"F7.wireOp",EDGE,"E67")])]})]});}
            var Q5;
            Q5=makeQuery(id+"F8.boolean.opBoolean","INTERSECT",EDGE,{"disambiguationData":[OD(0.0)],"derivedFrom":[makeQuery(id+"F5.opExtrude","SWEPT_FACE",FACE,{"disambiguationData":[OSD([sQuery(id+"F4.wireOp",EDGE,"E30")])]}),makeQuery(id+"F8.opExtrude","SWEPT_FACE",FACE,{"disambiguationData":[OSD([sQuery(id+"F7.wireOp",EDGE,"E67")])]})]});
            fillet(context, id + "F14", {"entities" : qUnion([Q0, Q1, Q2, Q3, Q4, Q5]), "radius" : 3 * mm, "tangentPropagation" : true, "allowEdgeOverflow" : false});
        }
        {
            var Q0;
            Q0=makeQuery(id+"F1.opExtrude","CAP_EDGE",EDGE,{"disambiguationData":[OSD([sQuery(id+"F0.wireOp",EDGE,"E1.bottom")])],"isStart":false});
            fillet(context, id + "F15", {"entities" : qUnion([Q0]), "radius" : 2 * mm, "tangentPropagation" : true, "allowEdgeOverflow" : false});
        }
        {
            var Q0;
            {var subQ0=sQuery(id+"F0.wireOp",EDGE,"E22.filletArc");var subQ1=sQuery(id+"F0.wireOp",EDGE,"E7");var subQ2=sQuery(id+"F0.wireOp",EDGE,"E6");var subQ3=sQuery(id+"F0.wireOp",EDGE,"E5");var subQ4=sQuery(id+"F0.wireOp",EDGE,"E4");var subQ5=sQuery(id+"F0.wireOp",EDGE,"E1.bottom");var subQ6=sQuery(id+"F0.wireOp",EDGE,"E21.filletArc");var subQ7=sQuery(id+"F0.wireOp",EDGE,"E1.top");var subQ8=sQuery(id+"F0.wireOp",EDGE,"E1.left");var subQ9=sQuery(id+"F0.wireOp",EDGE,"E1.right");var subQ10=sQuery(id+"F0.wireOp",EDGE,"E23.filletArc");var subQ11=sQuery(id+"F0.wireOp",EDGE,"E24.filletArc");Q0=makeQuery(id+"F2.boolean.opBoolean","SPLIT",FACE,{"disambiguationData":[TD([makeQuery(id+"F1.opExtrude","SWEPT_FACE",FACE,{"disambiguationData":[OSD([subQ5])]})])],"derivedFrom":makeQuery(id+"F1.opExtrude","CAP_FACE",FACE,{"disambiguationData":[OSD([subQ5,subQ7,subQ8,subQ9,subQ4,subQ3,subQ2,subQ1,subQ6,subQ0,subQ10,subQ11])],"isStart":true})});}
            var sketch = newSketch(context, id + "F16", { "sketchPlane" : qUnion([Q0])});
            skLineSegment(sketch, "E79", {"start": v(0, 90) * mm, "end": v(0, 120) * mm, "construction": true});
            skCircle(sketch, "E80", {"center": v(0, 120) * mm, "radius": 6 * mm});
            skArc(sketch, "E81", {"start": v(15, 120) * mm, "mid": v(0, 135) * mm, "end": v(-15, 120) * mm});
            skLineSegment(sketch, "E82", {"start": v(-15, 120) * mm, "end": v(-15, 108) * mm});
            skLineSegment(sketch, "E83", {"start": v(-15, 108) * mm, "end": v(-38, 90) * mm});
            skLineSegment(sketch, "E84", {"start": v(15, 120) * mm, "end": v(15, 108) * mm});
            skLineSegment(sketch, "E85", {"start": v(15, 108) * mm, "end": v(33, 90) * mm});
            skLineSegment(sketch, "E86", {"start": v(-80, 0) * mm, "end": v(80, 0) * mm, "construction": true});
            skArc(sketch, "E87.MirrorCS", {"start": v(15, -120) * mm, "mid": v(0, -135) * mm, "end": v(-15, -120) * mm});
            skLineSegment(sketch, "E88.MirrorCS", {"start": v(-15, -120) * mm, "end": v(-15, -108) * mm});
            skLineSegment(sketch, "E89.MirrorCS", {"start": v(-15, -108) * mm, "end": v(-38, -90) * mm});
            skLineSegment(sketch, "E90.MirrorCS", {"start": v(15, -120) * mm, "end": v(15, -108) * mm});
            skLineSegment(sketch, "E91.MirrorCS", {"start": v(15, -108) * mm, "end": v(33, -90) * mm});
            skCircle(sketch, "E92.MirrorC", {"center": v(0, -120) * mm, "radius": 6 * mm});
            skSolve(sketch);
        }
        {
            var Q0;
            Q0=makeQuery(id+"F16.imprint","IMPRINT",FACE,{"disambiguationData":[TD([[makeQuery(id+"F16.imprint","IMPRINT",EDGE,{"derivedFrom":sQuery(id+"F16.wireOp",EDGE,"E87.MirrorCS")}),-1.0]])]});
            var Q1;
            Q1=makeQuery(id+"F16.imprint","IMPRINT",FACE,{"disambiguationData":[TD([[makeQuery(id+"F16.imprint","IMPRINT",EDGE,{"derivedFrom":makeQuery(id+"F1.opExtrude","CAP_EDGE",EDGE,{"disambiguationData":[OSD([sQuery(id+"F0.wireOp",EDGE,"E1.left")])],"isStart":true})}),-1.0]])]});
            var Q2;
            Q2=makeQuery(id+"F16.imprint","IMPRINT",FACE,{"disambiguationData":[TD([[makeQuery(id+"F16.imprint","IMPRINT",EDGE,{"derivedFrom":sQuery(id+"F16.wireOp",EDGE,"E80")}),-1.0]])]});
            var Q3;
            Q3=makeQuery(id+"F2.opExtrude","CAP_FACE",FACE,{"disambiguationData":[OSD([sQuery(id+"F0.wireOp",EDGE,"E12"),sQuery(id+"F0.wireOp",EDGE,"E13"),sQuery(id+"F0.wireOp",EDGE,"E14"),sQuery(id+"F0.wireOp",EDGE,"E15"),sQuery(id+"F0.wireOp",EDGE,"E17.filletArc"),sQuery(id+"F0.wireOp",EDGE,"E18.filletArc"),sQuery(id+"F0.wireOp",EDGE,"E19.filletArc"),sQuery(id+"F0.wireOp",EDGE,"E20.filletArc"),sQuery(id+"F0.wireOp",EDGE,"E25.0"),sQuery(id+"F0.wireOp",EDGE,"E25.1"),sQuery(id+"F0.wireOp",EDGE,"E25.2"),sQuery(id+"F0.wireOp",EDGE,"E25.3"),sQuery(id+"F0.wireOp",EDGE,"E25.4"),sQuery(id+"F0.wireOp",EDGE,"E25.5"),sQuery(id+"F0.wireOp",EDGE,"E25.6"),sQuery(id+"F0.wireOp",EDGE,"E25.7")])],"isStart":false});
            extrude(context, id + "F17", {"entities" : qUnion([Q0, Q1, Q2]), "endBound" : BoundingType.UP_TO_SURFACE, "endBoundEntityFace" : qUnion([Q3]), "depth" : 25 * mm});
        }
    });
